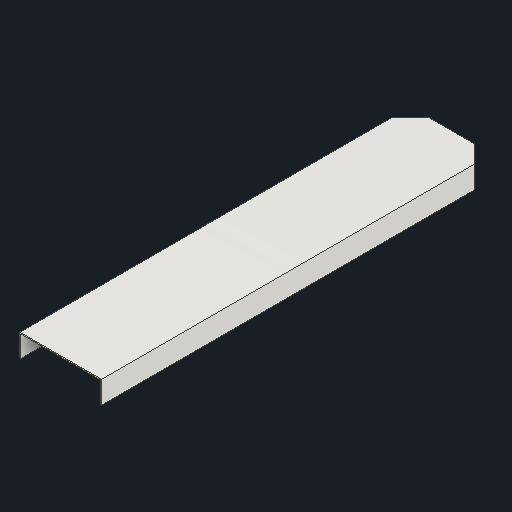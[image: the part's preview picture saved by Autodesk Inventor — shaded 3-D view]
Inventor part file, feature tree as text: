
AUTODESK INVENTOR PART (.ipt)
format: ipt  version: 2022 (Build 260153000, 153)  size: 129,536 bytes
history: native  units: mm
features: extrude x2, sketch x2, other x1, projected_geometry x1
ambient origin geometry x8: Origin, YZ Plane, XZ Plane, XY Plane, X Axis, Y Axis, Z Axis, Center Point
bodies: Body1 (feature_tree)
feature tree (6):
  other  "Sólido1"
  extrude  "Extrusión1"  Depth=230.0mm
  extrude  "Extrusión2"  Depth=60.0mm
  sketch  "Boceto1"  dims[d0=1100.0mm d1=230.0mm]
  sketch  "Boceto2"  dims[d2=50.0mm d3=50.0mm d4=50.0mm d5=50.0mm d6=3.0mm d7=0.0mm d8=2.5mm d9=60.0mm d10=0.0mm d11=30.0mm d12=30.0mm d13=300.0mm d14=500.0mm d15=100.0mm d16=100.0mm]
  projected_geometry  "Contorno proyectado1"
